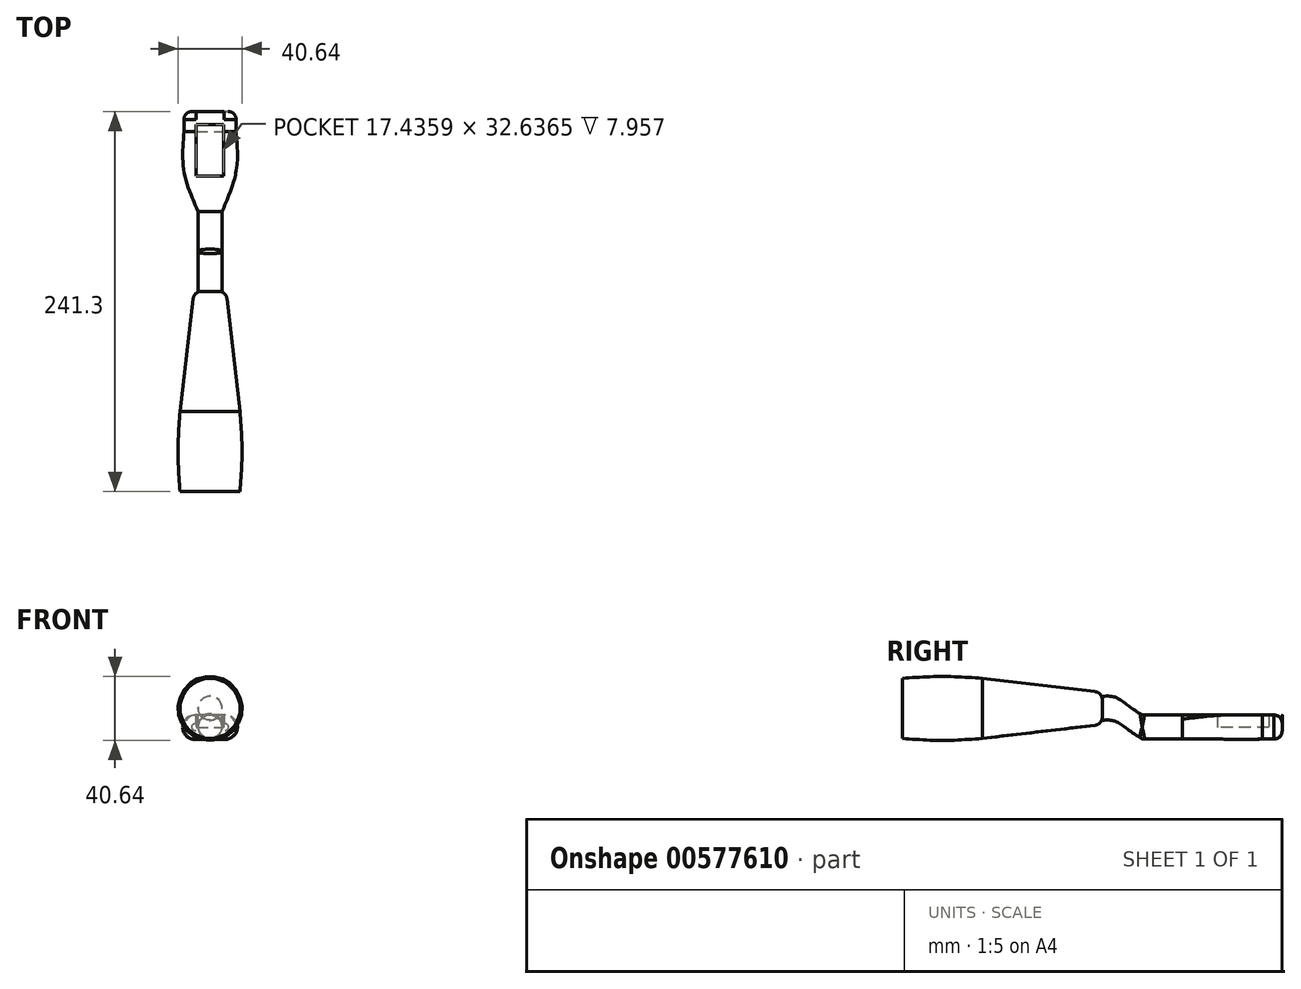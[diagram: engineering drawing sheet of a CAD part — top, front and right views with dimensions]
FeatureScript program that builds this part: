
annotation { "Feature Type Name" : "Feature", "Feature Type Description" : "" }
export const myFeature = defineFeature(function(context is Context, id is Id, definition is map)
    precondition{}
    {
        {
            var Q0;
            Q0=qCreatedBy(makeId("Front.planeOp"),FACE);
            cPlane(context, id + "F0", {"entities" : qUnion([Q0]), "cplaneType" : CPlaneType.OFFSET, "offset" : 50.8 * mm, "width" : 152.4 * mm, "height" : 152.4 * mm});
        }
        {
            var Q0;
            Q0=qCreatedBy(makeId("Front.planeOp"),FACE);
            cPlane(context, id + "F1", {"entities" : qUnion([Q0]), "cplaneType" : CPlaneType.OFFSET, "offset" : 25.4 * mm, "width" : 152.4 * mm, "height" : 152.4 * mm});
        }
        {
            var Q0;
            Q0=qCreatedBy(id+"F0.planeOp",FACE);
            var sketch = newSketch(context, id + "F2", { "sketchPlane" : qUnion([Q0])});
            skCircle(sketch, "E0", {"center": v(0, 0) * mm, "radius": 19.05 * mm});
            skSolve(sketch);
        }
        {
            var Q0;
            Q0=qCreatedBy(id+"F1.planeOp",FACE);
            var sketch = newSketch(context, id + "F3", { "sketchPlane" : qUnion([Q0])});
            skCircle(sketch, "E1", {"center": v(0, 0) * mm, "radius": 20.32 * mm});
            skSolve(sketch);
        }
        {
            var Q0;
            Q0=qCreatedBy(makeId("Front.planeOp"),FACE);
            var sketch = newSketch(context, id + "F4", { "sketchPlane" : qUnion([Q0])});
            skCircle(sketch, "E2", {"center": v(0, 0) * mm, "radius": 19.05 * mm});
            skSolve(sketch);
        }
        {
            var Q0;
            Q0=makeQuery(id+"F4.imprint","IMPRINT",FACE,{"disambiguationData":[TD([[makeQuery(id+"F4.imprint","IMPRINT",EDGE,{"derivedFrom":sQuery(id+"F4.wireOp",EDGE,"E2")}),1.0]])]});
            var Q1;
            Q1=makeQuery(id+"F3.imprint","IMPRINT",FACE,{"disambiguationData":[TD([[makeQuery(id+"F3.imprint","IMPRINT",EDGE,{"derivedFrom":sQuery(id+"F3.wireOp",EDGE,"E1")}),1.0]])]});
            var Q2;
            Q2=makeQuery(id+"F2.imprint","IMPRINT",FACE,{"disambiguationData":[TD([[makeQuery(id+"F2.imprint","IMPRINT",EDGE,{"derivedFrom":sQuery(id+"F2.wireOp",EDGE,"E0")}),1.0]])]});
            loft(context, id + "F5", {"sheetProfilesArray" : [{ "sheetProfileEntities" : qUnion([Q0]) }, { "sheetProfileEntities" : qUnion([Q1]) }, { "sheetProfileEntities" : qUnion([Q2]) }]});
        }
        {
            var Q0;
            Q0=qCreatedBy(makeId("Right.planeOp"),FACE);
            var sketch = newSketch(context, id + "F6", { "sketchPlane" : qUnion([Q0])});
            skArc(sketch, "E3", {"start": v(-51, 19.05) * mm, "mid": v(-64.46, 13.47) * mm, "end": v(-70.04, 0) * mm});
            skLineSegment(sketch, "E4", {"start": v(-51, 0) * mm, "end": v(-83, 0) * mm, "construction": true});
            skSolve(sketch);
        }
        {
            var Q0;
            Q0=sQuery(id+"F6.wireOp",EDGE,"E4");
            var Q1;
            Q1=sQuery(id+"F6.wireOp",EDGE,"E3");
            var Q2;
            Q2=sQuery(id+"F6.wireOp",EDGE,"E4");
            revolve(context, id + "F7", {"bodyType" : ToolBodyType.SURFACE, "surfaceEntities" : qUnion([Q0, Q1]), "axis" : qUnion([Q2]), "revolveType" : RevolveType.FULL});
        }
        {
            var Q0;
            Q0=qCreatedBy(makeId("Front.planeOp"),FACE);
            cPlane(context, id + "F8", {"entities" : qUnion([Q0]), "cplaneType" : CPlaneType.OFFSET, "offset" : 50.8 * mm, "oppositeDirection" : true, "width" : 152.4 * mm, "height" : 152.4 * mm});
        }
        {
            var Q0;
            Q0=qCreatedBy(id+"F8.planeOp",FACE);
            cPlane(context, id + "F9", {"entities" : qUnion([Q0]), "cplaneType" : CPlaneType.OFFSET, "offset" : 25.4 * mm, "oppositeDirection" : true, "width" : 152.4 * mm, "height" : 152.4 * mm});
        }
        {
            var Q0;
            Q0=qCreatedBy(id+"F9.planeOp",FACE);
            var sketch = newSketch(context, id + "F10", { "sketchPlane" : qUnion([Q0])});
            skCircle(sketch, "E5", {"center": v(0, 0) * mm, "radius": 10.16 * mm});
            skSolve(sketch);
        }
        {
            var Q1;
            Q1=makeQuery(id+"F10.imprint","IMPRINT",FACE,{"disambiguationData":[TD([[makeQuery(id+"F10.imprint","IMPRINT",EDGE,{"derivedFrom":sQuery(id+"F10.wireOp",EDGE,"E5")}),1.0]])]});
            var Q2;
            Q2=makeQuery(id+"F5.opLoft","CAP_FACE",FACE,{"disambiguationData":[OSD([makeQuery(id+"F4.imprint","IMPRINT",FACE,{"disambiguationData":[TD([[makeQuery(id+"F4.imprint","IMPRINT",EDGE,{"derivedFrom":sQuery(id+"F4.wireOp",EDGE,"E2")}),1.0]])]})])],"isStart":true});
            loft(context, id + "F11", {"operationType" : NewBodyOperationType.ADD, "sheetProfilesArray" : [{ "sheetProfileEntities" : qUnion([Q1]) }, { "sheetProfileEntities" : qUnion([Q2]) }]});
        }
        {
            var Q0;
            Q0=qCreatedBy(id+"F9.planeOp",FACE);
            cPlane(context, id + "F12", {"entities" : qUnion([Q0]), "cplaneType" : CPlaneType.OFFSET, "offset" : 25.4 * mm, "oppositeDirection" : true, "width" : 152.4 * mm, "height" : 152.4 * mm});
        }
        {
            var Q0;
            Q0=qCreatedBy(id+"F12.planeOp",FACE);
            var sketch = newSketch(context, id + "F13", { "sketchPlane" : qUnion([Q0])});
            skCircle(sketch, "E6", {"center": v(0, -11.85) * mm, "radius": 7.62 * mm});
            skSolve(sketch);
        }
        {
            var Q0;
            Q0=qCreatedBy(makeId("Right.planeOp"),FACE);
            var sketch = newSketch(context, id + "F14", { "sketchPlane" : qUnion([Q0])});
            skFitSpline(sketch, "E7", {"points": [v(76.26, 0) * mm, v(81.6, 0) * mm, v(86.55, -1.52) * mm, v(92.9, -6.1) * mm, v(101.54, -11.94) * mm], "startDerivative": vector(24.89, 1.27) * mm, "endDerivative": vector(29.5, -19.02) * mm});
            skSolve(sketch);
        }
        {
            var Q0;
            Q0=makeQuery(id+"F13.imprint","IMPRINT",FACE,{"disambiguationData":[TD([[makeQuery(id+"F13.imprint","IMPRINT",EDGE,{"derivedFrom":sQuery(id+"F13.wireOp",EDGE,"E6")}),1.0]])]});
            var Q1;
            Q1=sQuery(id+"F14.wireOp",EDGE,"E7");
            sweep(context, id + "F15", {"operationType" : NewBodyOperationType.ADD, "profiles" : qUnion([Q0]), "path" : qUnion([Q1]), "keepProfileOrientation" : true});
        }
        {
            var Q0;
            Q0=qCreatedBy(id+"F12.planeOp",FACE);
            cPlane(context, id + "F16", {"entities" : qUnion([Q0]), "cplaneType" : CPlaneType.OFFSET, "offset" : 25.4 * mm, "oppositeDirection" : true, "width" : 152.4 * mm, "height" : 152.4 * mm});
        }
        {
            var Q0;
            Q0=qCreatedBy(id+"F16.planeOp",FACE);
            var sketch = newSketch(context, id + "F17", { "sketchPlane" : qUnion([Q0])});
            skCircle(sketch, "E8.0", {"center": v(0, -11.85) * mm, "radius": 7.62 * mm});
            skSolve(sketch);
        }
        {
            var Q1;
            Q1=makeQuery(id+"F17.imprint","IMPRINT",FACE,{"disambiguationData":[TD([[makeQuery(id+"F17.imprint","IMPRINT",EDGE,{"derivedFrom":sQuery(id+"F17.wireOp",EDGE,"E8.0")}),1.0]])]});
            var Q2;
            Q2=makeQuery(id+"F15.opSweep","CAP_FACE",FACE,{"disambiguationData":[OSD([sQuery(id+"F13.wireOp",EDGE,"E6"),sQuery(id+"F14.wireOp",VERTEX,"E7.end")])],"isStart":true});
            loft(context, id + "F18", {"operationType" : NewBodyOperationType.ADD, "sheetProfilesArray" : [{ "sheetProfileEntities" : qUnion([Q1]) }, { "sheetProfileEntities" : qUnion([Q2]) }]});
        }
        {
            var Q0;
            {var subQ0=sQuery(id+"F14.wireOp",VERTEX,"E7.end");var subQ1=sQuery(id+"F13.wireOp",EDGE,"E6");Q0=makeQuery(id+"F18.boolean.opBoolean","MERGE",EDGE,{"derivedFrom":[makeQuery(id+"F15.opSweep","CAP_EDGE",EDGE,{"disambiguationData":[OSD([subQ1,subQ0])],"isStart":true}),makeQuery(id+"F18.opLoft","MID_CAP_EDGE",EDGE,{"disambiguationData":[OSD([subQ1,subQ0,sQuery(id+"F17.wireOp",EDGE,"E8.0")])],"capPos":1.0})]});}
            fillet(context, id + "F19", {"entities" : qUnion([Q0]), "radius" : 5.08 * mm, "tangentPropagation" : true, "allowEdgeOverflow" : false});
        }
        {
            var Q0;
            Q0=makeQuery(id+"F11.opLoft","CAP_FACE",FACE,{"disambiguationData":[OSD([makeQuery(id+"F10.imprint","IMPRINT",FACE,{"disambiguationData":[TD([[makeQuery(id+"F10.imprint","IMPRINT",EDGE,{"derivedFrom":sQuery(id+"F10.wireOp",EDGE,"E5")}),1.0]])]})])],"isStart":true});
            fillet(context, id + "F20", {"entities" : qUnion([Q0]), "radius" : 5.08 * mm, "tangentPropagation" : true, "allowEdgeOverflow" : false});
        }
        {
            var Q0;
            Q0=qCreatedBy(id+"F16.planeOp",FACE);
            cPlane(context, id + "F21", {"entities" : qUnion([Q0]), "cplaneType" : CPlaneType.OFFSET, "offset" : 25.4 * mm, "oppositeDirection" : true, "width" : 152.4 * mm, "height" : 152.4 * mm});
        }
        {
            var Q0;
            Q0=qCreatedBy(id+"F21.planeOp",FACE);
            cPlane(context, id + "F22", {"entities" : qUnion([Q0]), "cplaneType" : CPlaneType.OFFSET, "offset" : 25.4 * mm, "oppositeDirection" : true, "width" : 152.4 * mm, "height" : 152.4 * mm});
        }
        {
            var Q0;
            Q0=qCreatedBy(id+"F21.planeOp",FACE);
            var sketch = newSketch(context, id + "F23", { "sketchPlane" : qUnion([Q0])});
            skLineSegment(sketch, "E9.bottom", {"start": v(8.89, -4.23) * mm, "end": v(-8.89, -4.23) * mm});
            skLineSegment(sketch, "E9.top", {"start": v(8.89, -19.47) * mm, "end": v(-8.9, -19.47) * mm});
            skPoint(sketch, "E9.middle", {"position": v(0, -11.85) * mm});
            skArc(sketch, "E10", {"start": v(8.89, -19.47) * mm, "mid": v(16.5, -11.85) * mm, "end": v(8.9, -4.23) * mm});
            skArc(sketch, "E11", {"start": v(-8.9, -4.23) * mm, "mid": v(-16.51, -11.85) * mm, "end": v(-8.9, -19.47) * mm});
            skSolve(sketch);
        }
        {
            var Q0;
            Q0=qCreatedBy(id+"F22.planeOp",FACE);
            var sketch = newSketch(context, id + "F24", { "sketchPlane" : qUnion([Q0])});
            skLineSegment(sketch, "E12.0.0", {"start": v(-8.9, -19.47) * mm, "end": v(8.89, -19.47) * mm});
            skArc(sketch, "E12.0.1", {"start": v(8.89, -19.47) * mm, "mid": v(16.5, -11.85) * mm, "end": v(8.9, -4.23) * mm});
            skLineSegment(sketch, "E12.0.2", {"start": v(8.89, -4.23) * mm, "end": v(-8.89, -4.23) * mm});
            skArc(sketch, "E12.0.3", {"start": v(-8.89, -4.23) * mm, "mid": v(-16.51, -11.85) * mm, "end": v(-8.9, -19.47) * mm});
            skSolve(sketch);
        }
        {
            var Q0;
            Q0=makeQuery(id+"F18.opLoft","CAP_FACE",FACE,{"disambiguationData":[OSD([makeQuery(id+"F17.imprint","IMPRINT",FACE,{"disambiguationData":[TD([[makeQuery(id+"F17.imprint","IMPRINT",EDGE,{"derivedFrom":sQuery(id+"F17.wireOp",EDGE,"E8.0")}),1.0]])]})])],"isStart":true});
            var Q1;
            Q1=makeQuery(id+"F23.imprint","IMPRINT",FACE,{"disambiguationData":[TD([[makeQuery(id+"F23.imprint","IMPRINT",EDGE,{"derivedFrom":sQuery(id+"F23.wireOp",EDGE,"E9.bottom")}),1.0]])]});
            var Q2;
            Q2=makeQuery(id+"F24.imprint","IMPRINT",FACE,{"disambiguationData":[TD([[makeQuery(id+"F24.imprint","IMPRINT",EDGE,{"derivedFrom":sQuery(id+"F24.wireOp",EDGE,"E12.0.0")}),1.0]])]});
            loft(context, id + "F25", {"sheetProfilesArray" : [{ "sheetProfileEntities" : qUnion([Q0]) }, { "sheetProfileEntities" : qUnion([Q1]) }, { "sheetProfileEntities" : qUnion([Q2]) }]});
        }
        {
            var Q0;
            Q0=qCreatedBy(id+"F22.planeOp",FACE);
            cPlane(context, id + "F26", {"entities" : qUnion([Q0]), "cplaneType" : CPlaneType.OFFSET, "offset" : 12.7 * mm, "oppositeDirection" : true, "width" : 152.4 * mm, "height" : 152.4 * mm});
        }
        {
            var Q0;
            Q0=qCreatedBy(id+"F26.planeOp",FACE);
            var sketch = newSketch(context, id + "F27", { "sketchPlane" : qUnion([Q0])});
            skFitSpline(sketch, "E13.0.0", {"points": [v(-8.89, -4.23) * mm, v(-2.96, -4.23) * mm, v(2.96, -4.23) * mm, v(8.9, -4.23) * mm]});
            skFitSpline(sketch, "E13.0.1", {"points": [v(8.9, -4.23) * mm, v(9.4, -4.23) * mm, v(10.39, -4.33) * mm, v(12.3, -4.91) * mm, v(14.42, -6.33) * mm, v(16.11, -8.86) * mm, v(16.7, -11.85) * mm, v(16.11, -14.85) * mm, v(14.7, -16.96) * mm, v(13.15, -18.23) * mm, v(11.83, -18.94) * mm, v(10.39, -19.38) * mm, v(9.4, -19.47) * mm, v(8.89, -19.47) * mm]});
            skFitSpline(sketch, "E13.0.2", {"points": [v(8.89, -19.47) * mm, v(2.96, -19.47) * mm, v(-2.96, -19.47) * mm, v(-8.9, -19.47) * mm]});
            skFitSpline(sketch, "E13.0.3", {"points": [v(-8.9, -19.47) * mm, v(-9.4, -19.47) * mm, v(-10.39, -19.38) * mm, v(-12.3, -18.8) * mm, v(-14.42, -17.38) * mm, v(-16.11, -14.85) * mm, v(-16.7, -11.85) * mm, v(-16.11, -8.86) * mm, v(-14.7, -6.75) * mm, v(-13.15, -5.48) * mm, v(-11.83, -4.77) * mm, v(-10.39, -4.33) * mm, v(-9.4, -4.23) * mm, v(-8.89, -4.23) * mm]});
            skSolve(sketch);
        }
        {
            var Q1;
            Q1=makeQuery(id+"F27.imprint","IMPRINT",FACE,{"disambiguationData":[TD([[makeQuery(id+"F27.imprint","IMPRINT",EDGE,{"derivedFrom":sQuery(id+"F27.wireOp",EDGE,"E13.0.0")}),-1.0]])]});
            var Q2;
            Q2=makeQuery(id+"F25.opLoft","CAP_FACE",FACE,{"disambiguationData":[OSD([makeQuery(id+"F24.imprint","IMPRINT",FACE,{"disambiguationData":[TD([[makeQuery(id+"F24.imprint","IMPRINT",EDGE,{"derivedFrom":sQuery(id+"F24.wireOp",EDGE,"E12.0.0")}),1.0]])]})])],"isStart":true});
            loft(context, id + "F28", {"operationType" : NewBodyOperationType.ADD, "sheetProfilesArray" : [{ "sheetProfileEntities" : qUnion([Q1]) }, { "sheetProfileEntities" : qUnion([Q2]) }]});
        }
        {
            var Q0;
            Q0=makeQuery(id+"F28.opLoft","CAP_FACE",FACE,{"disambiguationData":[OSD([makeQuery(id+"F27.imprint","IMPRINT",FACE,{"disambiguationData":[TD([[makeQuery(id+"F27.imprint","IMPRINT",EDGE,{"derivedFrom":sQuery(id+"F27.wireOp",EDGE,"E13.0.0")}),-1.0]])]})])],"isStart":true});
            fillet(context, id + "F29", {"entities" : qUnion([Q0]), "radius" : 5.08 * mm, "tangentPropagation" : true, "allowEdgeOverflow" : false});
        }
        {
            var Q0;
            Q0=qCreatedBy(makeId("Top.planeOp"),FACE);
            cPlane(context, id + "F30", {"entities" : qUnion([Q0]), "cplaneType" : CPlaneType.OFFSET, "offset" : 12.2 * mm, "oppositeDirection" : true, "width" : 152.4 * mm, "height" : 152.4 * mm});
        }
        {
            var Q0;
            Q0=qCreatedBy(id+"F30.planeOp",FACE);
            var sketch = newSketch(context, id + "F31", { "sketchPlane" : qUnion([Q0])});
            skLineSegment(sketch, "E14.bottom", {"start": v(-8.84, 182.16) * mm, "end": v(8.6, 182.16) * mm});
            skLineSegment(sketch, "E14.top", {"start": v(-8.84, 149.52) * mm, "end": v(8.6, 149.52) * mm});
            skLineSegment(sketch, "E14.left", {"start": v(-8.84, 182.16) * mm, "end": v(-8.84, 149.52) * mm});
            skLineSegment(sketch, "E14.right", {"start": v(8.6, 182.16) * mm, "end": v(8.6, 149.52) * mm});
            skSolve(sketch);
        }
        {
            var Q0;
            Q0 = qSketchRegion(id + "F31", true);
            extrude(context, id + "F32", {"entities" : qUnion([Q0]), "operationType" : NewBodyOperationType.REMOVE, "depth" : 25.4 * mm, "offsetDistance" : 25.4 * mm});
        }
    });
